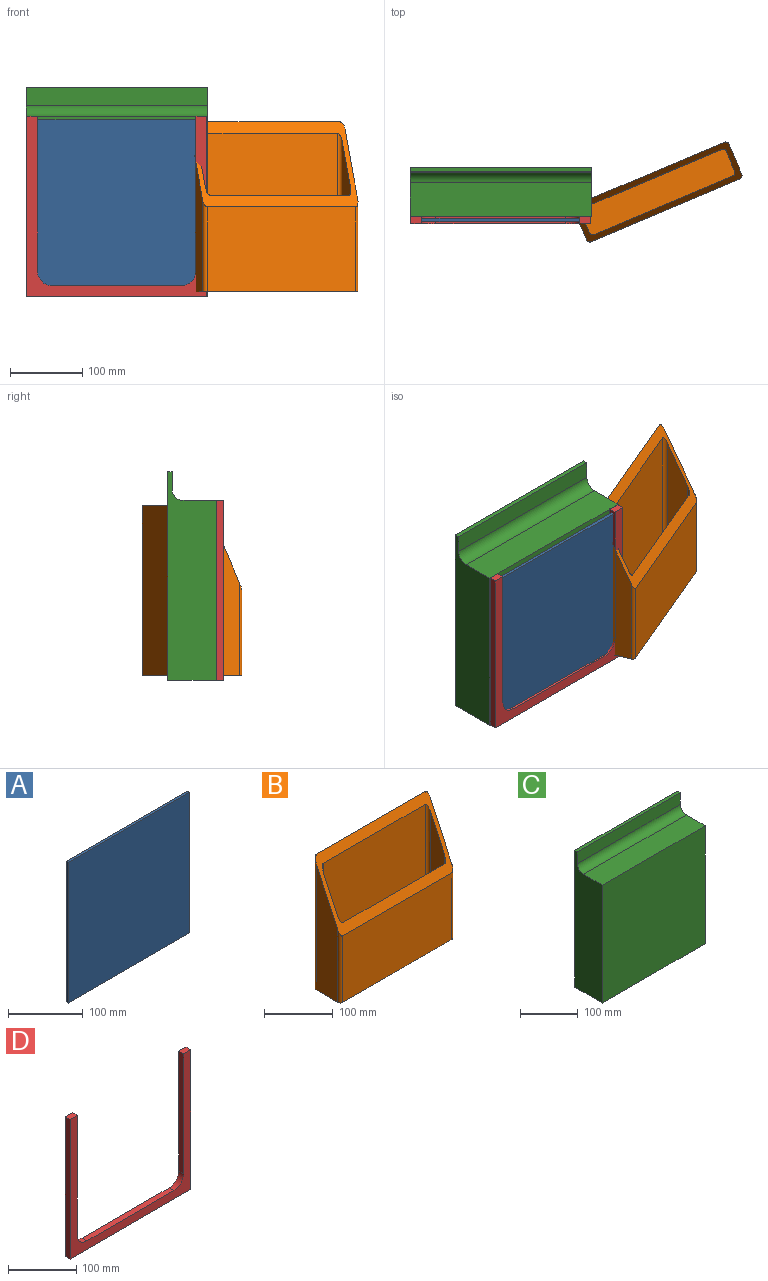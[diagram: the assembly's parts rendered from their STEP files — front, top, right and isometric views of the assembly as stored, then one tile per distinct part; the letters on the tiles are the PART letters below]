
ASSEMBLY  parts=4 mates=3
PART A: 6 faces, bbox 230x4x230 mm
  f0: plane 230x4mm, normal (0,0,1), area 920mm2, adj f1,f3,f4,f5
  f1: plane 230x4mm, normal (-1,0,0), area 920mm2, adj f0,f2,f4,f5
  f2: plane 230x4mm, normal (0,0,-1), area 920mm2, adj f1,f3,f4,f5
  f3: plane 230x4mm, normal (1,0,0), area 920mm2, adj f0,f2,f4,f5
  f4: plane 230x230mm, normal (0,-1,0), area 52900mm2, adj f0,f1,f2,f3
  f5: plane 230x230mm, normal (0,1,0), area 52900mm2, adj f0,f1,f2,f3
PART B: 23 faces, bbox 234x59x236 mm
  f0: plane 236x224mm, normal (0,1,0), area 52763.5mm2, adj f2,f5,f15,f16,f19,f21
  f1: plane 225.28x45mm, normal (-1,0,0), area 7966.2mm2, adj f2,f5,f15,f17
  f2: plane 234x55mm, normal (0,0,-1), area 12848.5mm2, adj f0,f1,f3,f4,f15,f16,f17,f18
  f3: plane 225.28x45mm, normal (1,0,0), area 7966.2mm2, adj f2,f5,f16,f18
  f4: plane 224x118.05mm, normal (0,-1,0), area 26443.7mm2, adj f2,f5,f17,f18
  f5: plane 234x117.95mm, normal (0,-0.91,0.42), area 9725.1mm2, adj f0,f1,f3,f4,f7,f8,f9,f10
  f6: plane 219x40mm, normal (0,0,1), area 8738.5mm2, adj f7,f8,f9,f10,f11,f12,f13,f14
  f7: plane 212.42x209mm, normal (0,-1,0), area 44395mm2, adj f5,f6,f11,f12
  f8: plane 209x126.64mm, normal (0,1,0), area 26466.9mm2, adj f5,f6,f13,f14
  f9: plane 201.69x30mm, normal (-1,0,0), area 5085.8mm2, adj f5,f6,f11,f13
  f10: plane 201.69x30mm, normal (1,0,0), area 5085.8mm2, adj f5,f6,f12,f14
  f11: cylinder r=5mm len=212.42mm, axis (0,0,-1), area 1637.7mm2, adj f5,f6,f7,f9
  f12: cylinder r=5mm len=212.42mm, axis (0,0,1), area 1637.7mm2, adj f5,f6,f7,f10
  f13: cylinder r=5mm len=137.36mm, axis (0,0,1), area 1025.2mm2, adj f5,f6,f8,f9
  f14: cylinder r=5mm len=137.36mm, axis (0,0,-1), area 1025.2mm2, adj f5,f6,f8,f10
  f15: cylinder r=5mm len=236mm, axis (0,0,-1), area 1822.9mm2, adj f0,f1,f2,f5
  f16: cylinder r=5mm len=236mm, axis (0,0,1), area 1822.9mm2, adj f0,f2,f3,f5
  f17: cylinder r=5mm len=128.77mm, axis (0,0,1), area 957.8mm2, adj f1,f2,f4,f5
  f18: cylinder r=5mm len=128.77mm, axis (0,0,-1), area 957.8mm2, adj f2,f3,f4,f5
  f19: cylinder r=4mm len=8mm, axis (0,-1,0), area 100.5mm2, adj f0,f20
  f20: plane 8x8mm, normal (0,1,0), area 50.3mm2, adj f19
  f21: cylinder r=4mm len=8mm, axis (0,-1,0), area 100.5mm2, adj f0,f22
  f22: plane 8x8mm, normal (0,1,0), area 50.3mm2, adj f21
PART C: 31 faces, bbox 252x67.7x290 mm
  f0: plane 32x4mm, normal (0,0,-1), area 128mm2, adj f1,f11,f12,f14
  f1: plane 290x252mm, normal (0,1,0), area 72292.8mm2, adj f0,f3,f4,f7,f9,f10,f12,f13
  f2: plane 252x46.35mm, normal (0,0,1), area 11680.2mm2, adj f3,f5,f8,f16
  f3: plane 290x67.7mm, normal (-1,0,0), area 17227.3mm2, adj f1,f2,f4,f5,f6,f7,f8
  f4: plane 252x67.7mm, normal (0,0,-1), area 17060.4mm2, adj f1,f3,f5,f16
  f5: plane 252x250mm, normal (0,-1,0), area 63000mm2, adj f2,f3,f4,f16
  f6: plane 252x25mm, normal (0,-1,0), area 6300mm2, adj f3,f7,f8,f16
  f7: plane 252x6.35mm, normal (0,0,1), area 1600.2mm2, adj f1,f3,f6,f16
  f8: cylinder r=15mm len=252mm, axis (1,0,0), area 5937.6mm2, adj f2,f3,f6,f16
  f9: plane 32x4mm, normal (0,0,-1), area 128mm2, adj f1,f11,f13,f14
  f10: plane 70x4mm, normal (0,0,1), area 280mm2, adj f1,f11,f12,f13
  f11: plane 80x12mm, normal (0,1,0), area 787.2mm2, adj f0,f9,f10,f12,f13,f14
  f12: cylinder r=5mm len=10mm, axis (0,-1,0), area 62.8mm2, adj f0,f1,f10,f11
  f13: cylinder r=5mm len=10mm, axis (0,-1,0), area 62.8mm2, adj f1,f9,f10,f11
  f14: cylinder r=3.25mm len=6mm, axis (0,1,0), area 30.6mm2, adj f0,f1,f9,f11
  f15: plane 8x4mm, normal (-1,0,0), area 32mm2, adj f24,f25,f26,f27
  f16: plane 290x67.7mm, normal (1,0,0), area 4175.8mm2, adj f1,f2,f4,f5,f6,f7,f8,f27
  f17: plane 8x4mm, normal (-1,0,0), area 32mm2, adj f21,f22,f23,f27
  f18: plane 237.3x55mm, normal (1,0,0), area 13051.5mm2, adj f27,f28,f29,f30
  f19: cylinder r=4mm len=8mm, axis (0,-1,0), area 50.3mm2, adj f21,f22,f23,f27
  f20: cylinder r=4mm len=8mm, axis (0,-1,0), area 50.3mm2, adj f24,f25,f26,f27
  f21: plane 232.68x4mm, normal (0,0,1), area 930.7mm2, adj f17,f19,f22,f27
  f22: plane 236.68x8mm, normal (0,-1,0), area 1886.5mm2, adj f17,f19,f21,f23
  f23: plane 232.68x4mm, normal (0,0,-1), area 930.7mm2, adj f17,f19,f22,f27
  f24: plane 232.68x4mm, normal (0,0,1), area 930.7mm2, adj f15,f20,f26,f27
  f25: plane 232.68x4mm, normal (0,0,-1), area 930.7mm2, adj f15,f20,f26,f27
  f26: plane 236.68x8mm, normal (0,-1,0), area 1886.5mm2, adj f15,f20,f24,f25
  f27: plane 245.65x237.3mm, normal (0,-1,0), area 54519.7mm2, adj f15,f16,f17,f18,f19,f20,f21,f23
  f28: plane 245.65x55mm, normal (0,0,-1), area 13510.7mm2, adj f16,f18,f27,f29
  f29: plane 245.65x237.3mm, normal (0,1,0), area 58292.7mm2, adj f16,f18,f28,f30
  f30: plane 245.65x55mm, normal (0,0,1), area 13510.7mm2, adj f16,f18,f27,f29
PART D: 12 faces, bbox 250x10x250 mm
  f0: plane 215x10mm, normal (1,0,0), area 2150mm2, adj f1,f8,f9,f11
  f1: plane 15x10mm, normal (0,0,1), area 150mm2, adj f0,f2,f8,f9
  f2: plane 250x10mm, normal (-1,0,0), area 2500mm2, adj f1,f3,f8,f9
  f3: plane 250x10mm, normal (0,0,-1), area 2500mm2, adj f2,f4,f8,f9
  f4: plane 250x10mm, normal (1,0,0), area 2500mm2, adj f3,f5,f8,f9
  f5: plane 15x10mm, normal (0,0,1), area 150mm2, adj f4,f6,f8,f9
  f6: plane 215x10mm, normal (-1,0,0), area 2150mm2, adj f5,f8,f9,f10
  f7: plane 180x10mm, normal (0,0,1), area 1800mm2, adj f8,f9,f10,f11
  f8: plane 250x250mm, normal (0,-1,0), area 10971.7mm2, adj f0,f1,f2,f3,f4,f5,f6,f7
  f9: plane 250x250mm, normal (0,1,0), area 10971.7mm2, adj f0,f1,f2,f3,f4,f5,f6,f7
  f10: cylinder r=20mm len=20mm, axis (0,1,0), area 314.2mm2, adj f6,f7,f8,f9
  f11: cylinder r=20mm len=20mm, axis (0,-1,0), area 314.2mm2, adj f0,f7,f8,f9
PLACE A rot(axis=(1,0,0),180deg) t=(351.58,-193.08,-305.53)mm
PLACE B rot(axis=(0,0,1),22.9deg) t=(243.79,-83.79,-311.18)mm
PLACE C t=(350.58,-50.68,-310.53)mm
PLACE D t=(351.58,-50.68,-310.53)mm
MATE fastened D.f7 <-> A.f0  axis (0,0,1) through (351.58,-123.38,-420.53)mm
MATE fastened D.f9 <-> C.f5  axis (0,1,0) through (351.58,-118.38,-435.53)mm
MATE planar B.f2 <-> C.f30  axis (0,0,-1) through (569.76,-84.53,-429.18)mm
